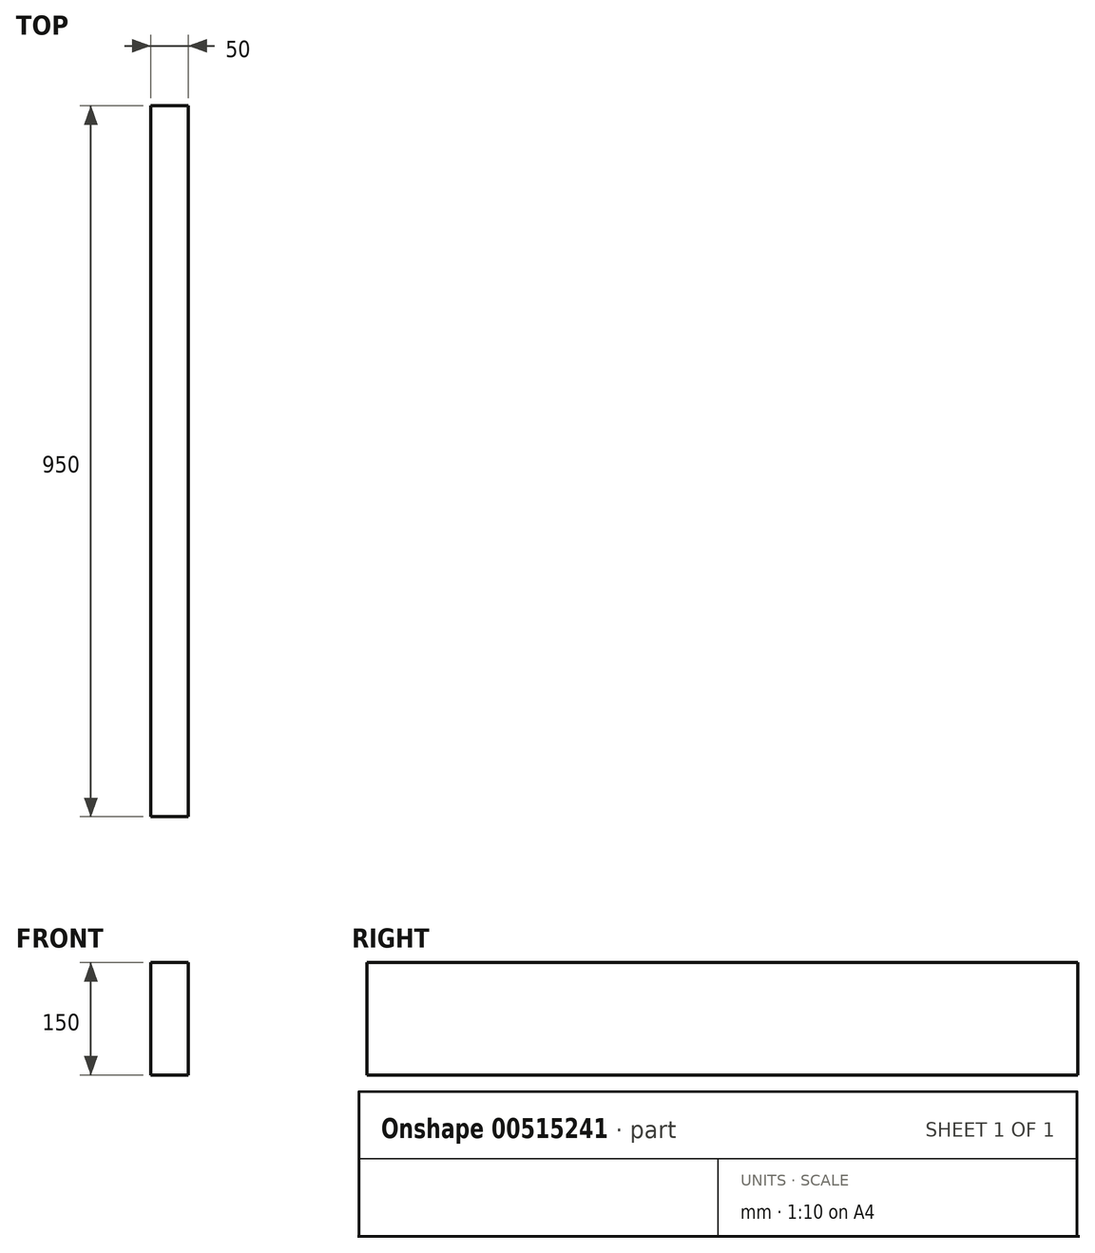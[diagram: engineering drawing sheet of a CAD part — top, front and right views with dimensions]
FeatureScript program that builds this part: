
annotation { "Feature Type Name" : "Feature", "Feature Type Description" : "" }
export const myFeature = defineFeature(function(context is Context, id is Id, definition is map)
    precondition{}
    {
        {
            var Q0;
            Q0=qCreatedBy(makeId("Front.planeOp"),FACE);
            var sketch = newSketch(context, id + "F0", { "sketchPlane" : qUnion([Q0])});
            skLineSegment(sketch, "E0.bottom", {"start": v(25, -75) * mm, "end": v(-25, -75) * mm});
            skLineSegment(sketch, "E0.top", {"start": v(25, 75) * mm, "end": v(-25, 75) * mm});
            skLineSegment(sketch, "E0.left", {"start": v(25, -75) * mm, "end": v(25, 75) * mm});
            skLineSegment(sketch, "E0.right", {"start": v(-25, -75) * mm, "end": v(-25, 75) * mm});
            skPoint(sketch, "E0.middle", {"position": v(0, 0) * mm});
            skSolve(sketch);
        }
        {
            var Q0;
            Q0=makeQuery(id+"F0.imprint","IMPRINT",FACE,{"disambiguationData":[TD([[makeQuery(id+"F0.imprint","IMPRINT",EDGE,{"derivedFrom":sQuery(id+"F0.wireOp",EDGE,"E0.bottom")}),-1.0]])]});
            extrude(context, id + "F1", {"entities" : qUnion([Q0]), "depth" : 450 * mm, "offsetDistance" : 25 * mm, "hasSecondDirection" : true, "secondDirectionOppositeDirection" : true, "secondDirectionDepth" : 500 * mm});
        }
    });
